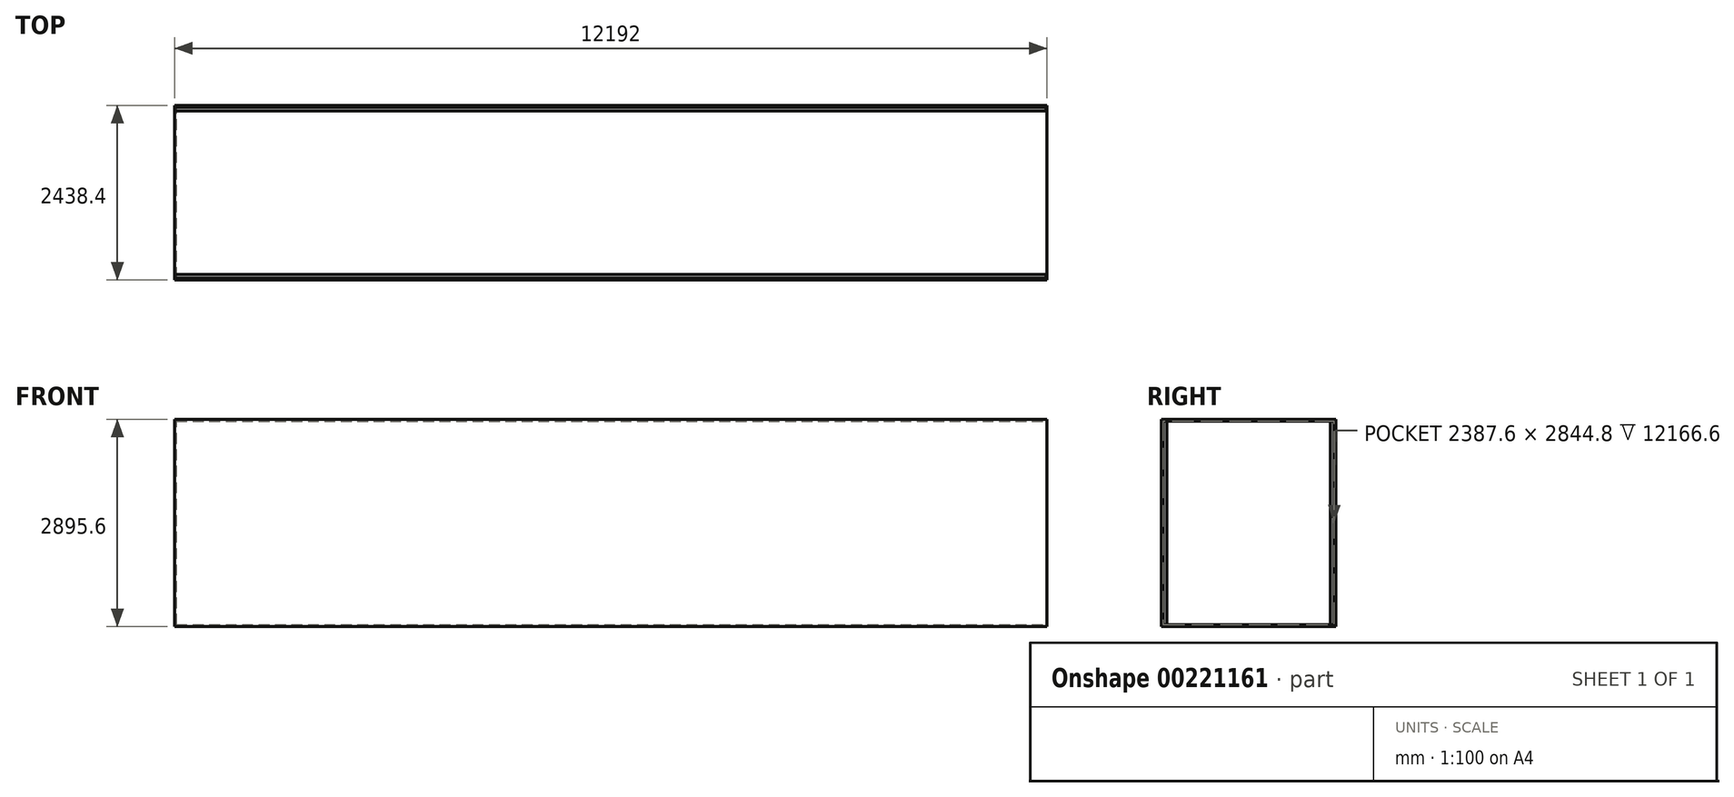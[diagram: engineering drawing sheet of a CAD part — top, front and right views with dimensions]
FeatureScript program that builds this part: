
annotation { "Feature Type Name" : "Feature", "Feature Type Description" : "" }
export const myFeature = defineFeature(function(context is Context, id is Id, definition is map)
    precondition{}
    {
        {
            var Q0;
            Q0=qCreatedBy(makeId("Front.planeOp"),FACE);
            var sketch = newSketch(context, id + "F0", { "sketchPlane" : qUnion([Q0])});
            skLineSegment(sketch, "E0.bottom", {"start": v(-4375.98, -2895.6) * mm, "end": v(7816.02, -2895.6) * mm});
            skLineSegment(sketch, "E0.top", {"start": v(-4375.98, 0) * mm, "end": v(7816.02, 0) * mm});
            skLineSegment(sketch, "E0.left", {"start": v(-4375.98, -2895.6) * mm, "end": v(-4375.98, 0) * mm});
            skLineSegment(sketch, "E0.right", {"start": v(7816.02, -2895.6) * mm, "end": v(7816.02, 0) * mm});
            skSolve(sketch);
        }
        {
            var Q0;
            Q0=makeQuery(id+"F0.imprint","IMPRINT",FACE,{"disambiguationData":[TD([[makeQuery(id+"F0.imprint","IMPRINT",EDGE,{"derivedFrom":sQuery(id+"F0.wireOp",EDGE,"E0.bottom")}),1.0]])]});
            extrude(context, id + "F1", {"entities" : qUnion([Q0]), "depth" : 2438.4 * mm});
        }
        {
            var Q0;
            Q0=makeQuery(id+"F1.opExtrude","SWEPT_FACE",FACE,{"disambiguationData":[OSD([sQuery(id+"F0.wireOp",EDGE,"E0.right")])]});
            shell(context, id + "F2", {"entities" : qUnion([Q0]), "thickness" : 25.4 * mm});
        }
        {
            var Q0;
            Q0=makeQuery(id+"F0.imprint","IMPRINT",FACE,{"disambiguationData":[TD([[makeQuery(id+"F0.imprint","IMPRINT",EDGE,{"derivedFrom":sQuery(id+"F0.wireOp",EDGE,"E0.bottom")}),1.0]])]});
            cPlane(context, id + "F3", {"entities" : qUnion([Q0]), "cplaneType" : CPlaneType.OFFSET, "offset" : 25.4 * mm, "width" : 152.4 * mm, "height" : 152.4 * mm});
        }
        {
            var Q0;
            Q0=qCreatedBy(id+"F3.planeOp",FACE);
            var sketch = newSketch(context, id + "F4", { "sketchPlane" : qUnion([Q0])});
            skLineSegment(sketch, "E1.bottom", {"start": v(-4372.72, 0) * mm, "end": v(7803.63, 0) * mm});
            skLineSegment(sketch, "E1.top", {"start": v(-4372.72, -2880.85) * mm, "end": v(7803.63, -2880.85) * mm});
            skLineSegment(sketch, "E1.left", {"start": v(-4372.72, 0) * mm, "end": v(-4372.72, -2880.85) * mm});
            skLineSegment(sketch, "E1.right", {"start": v(7803.63, 0) * mm, "end": v(7803.63, -2880.85) * mm});
            skSolve(sketch);
        }
        {
            var Q0;
            Q0 = qSketchRegion(id + "F4", true);
            extrude(context, id + "F5", {"entities" : qUnion([Q0]), "depth" : 50.8 * mm});
        }
        {
            var Q0;
            Q0=qCreatedBy(id+"F3.planeOp",FACE);
            cPlane(context, id + "F6", {"entities" : qUnion([Q0]), "cplaneType" : CPlaneType.OFFSET, "offset" : 1193.8 * mm, "width" : 152.4 * mm, "height" : 152.4 * mm});
        }
        {
            var Q0;
            Q0=makeQuery(id+"F5.opExtrude","SWEPT_BODY",BODY,{"disambiguationData":[OSD([sQuery(id+"F4.wireOp",EDGE,"E1.bottom"),sQuery(id+"F4.wireOp",EDGE,"E1.top"),sQuery(id+"F4.wireOp",EDGE,"E1.left"),sQuery(id+"F4.wireOp",EDGE,"E1.right")])]});
            var Q1;
            Q1=qCreatedBy(id+"F6.planeOp",FACE);
            mirror(context, id + "F7", {"entities" : qUnion([Q0]), "mirrorPlane" : qUnion([Q1])});
        }
    });
